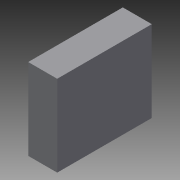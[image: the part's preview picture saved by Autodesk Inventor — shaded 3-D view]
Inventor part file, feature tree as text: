
AUTODESK INVENTOR PART (.ipt)
format: ipt  version: 2015 (Build 190159000, 159)  size: 68,608 bytes
history: native  units: mm
features: extrude x1, sketch x1
ambient origin geometry x8: Origin, YZ Plane, XZ Plane, XY Plane, X Axis, Y Axis, Z Axis, Center Point
bodies: Solid1 (feature_tree)
feature tree (2):
  extrude  "Extrusion1"  Depth=81.5mm
  sketch  "Sketch1"  dims[d0=70.0mm d1=81.5mm d2=25.0mm d3=0.0mm]
